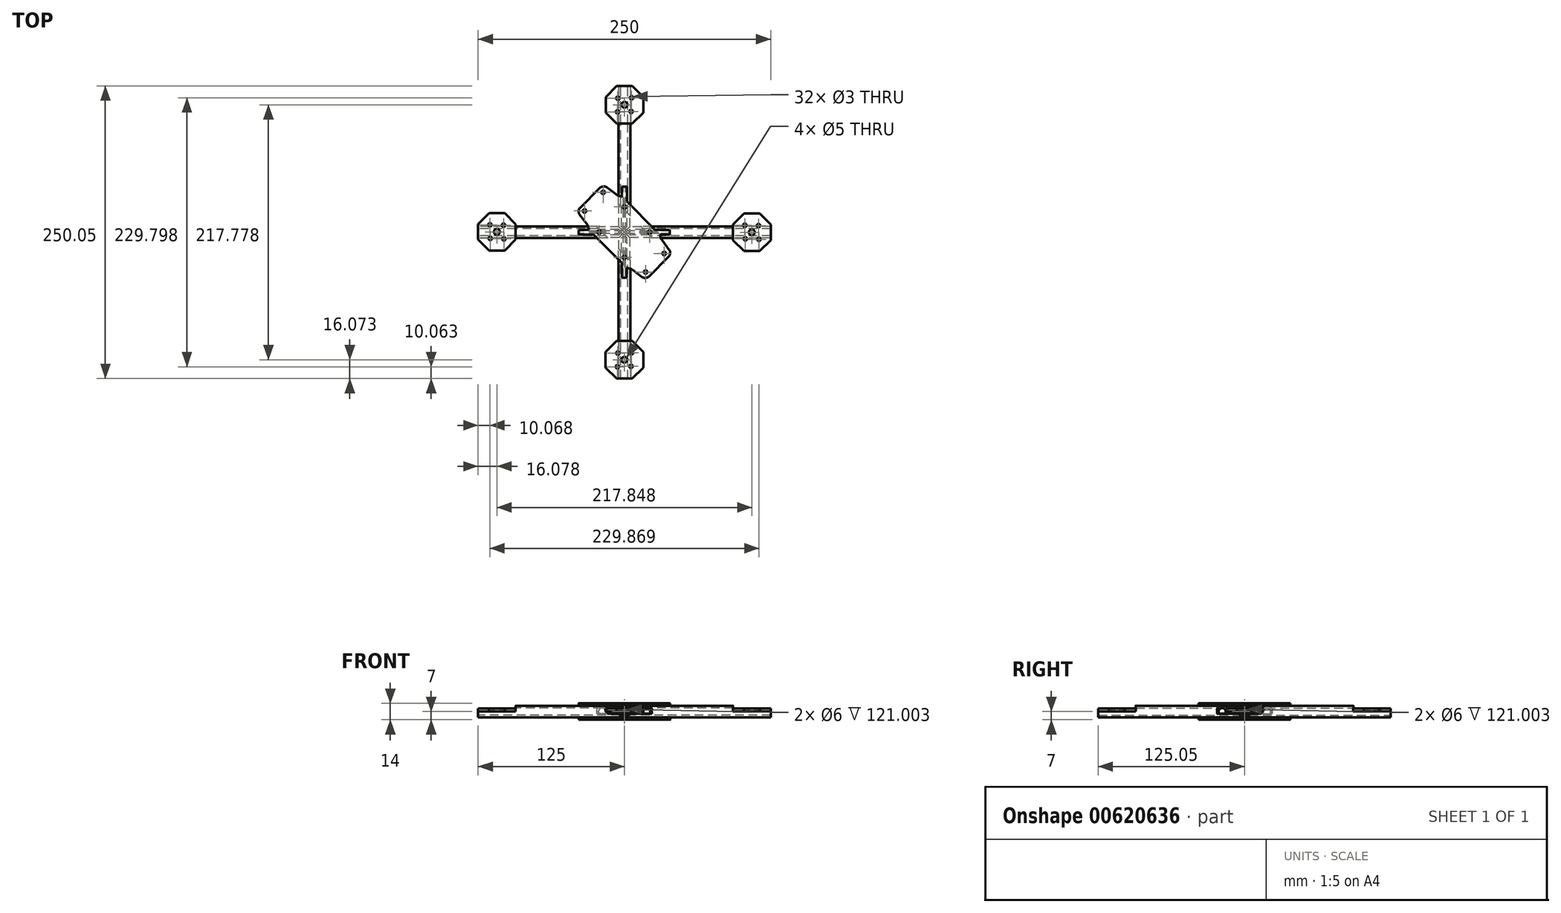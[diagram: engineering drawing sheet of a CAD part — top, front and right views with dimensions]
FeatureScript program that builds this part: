
annotation { "Feature Type Name" : "Feature", "Feature Type Description" : "" }
export const myFeature = defineFeature(function(context is Context, id is Id, definition is map)
    precondition{}
    {
        {
            var Q0;
            Q0=qCreatedBy(makeId("Front.planeOp"),FACE);
            var sketch = newSketch(context, id + "F0", { "sketchPlane" : qUnion([Q0])});
            skCircle(sketch, "E0", {"center": v(0, 0) * mm, "radius": 5 * mm});
            skCircle(sketch, "E1", {"center": v(0, 0) * mm, "radius": 3 * mm});
            skSolve(sketch);
        }
        {
            var Q0;
            Q0 = qSketchRegion(id + "F0", true);
            extrude(context, id + "F1", {"entities" : qUnion([Q0]), "endBound" : BoundingType.SYMMETRIC, "depth" : 250 * mm, "offsetDistance" : 25.4 * mm});
        }
        {
            var Q0;
            Q0=qCreatedBy(makeId("Right.planeOp"),FACE);
            var sketch = newSketch(context, id + "F2", { "sketchPlane" : qUnion([Q0])});
            skCircle(sketch, "E2", {"center": v(0, 0) * mm, "radius": 5 * mm});
            skCircle(sketch, "E3", {"center": v(0, 0) * mm, "radius": 3 * mm});
            skSolve(sketch);
        }
        {
            var Q0;
            Q0 = qSketchRegion(id + "F2", true);
            extrude(context, id + "F3", {"entities" : qUnion([Q0]), "operationType" : NewBodyOperationType.ADD, "endBound" : BoundingType.SYMMETRIC, "depth" : 250 * mm, "offsetDistance" : 25.4 * mm});
        }
        {
            var Q0;
            Q0=qCreatedBy(makeId("Top.planeOp"),FACE);
            var sketch = newSketch(context, id + "F4", { "sketchPlane" : qUnion([Q0])});
            skLineSegment(sketch, "E4.bottom", {"start": v(-92.85, 5) * mm, "end": v(-125.01, 5) * mm});
            skLineSegment(sketch, "E4.top", {"start": v(-92.85, -5) * mm, "end": v(-125.01, -5) * mm});
            skLineSegment(sketch, "E4.left", {"start": v(-92.85, 5) * mm, "end": v(-92.85, -5) * mm});
            skLineSegment(sketch, "E4.right", {"start": v(-125.01, 5) * mm, "end": v(-125.01, -5) * mm});
            skPoint(sketch, "E4.middle", {"position": v(-108.93, 0) * mm});
            skLineSegment(sketch, "E5.bottom", {"start": v(125.05, 5) * mm, "end": v(92.89, 5) * mm});
            skLineSegment(sketch, "E5.top", {"start": v(125.05, -5) * mm, "end": v(92.89, -5) * mm});
            skLineSegment(sketch, "E5.left", {"start": v(125.05, 5) * mm, "end": v(125.05, -5) * mm});
            skLineSegment(sketch, "E5.right", {"start": v(92.89, 5) * mm, "end": v(92.89, -5) * mm});
            skPoint(sketch, "E5.middle", {"position": v(108.97, 0) * mm});
            skLineSegment(sketch, "E6.bottom", {"start": v(-5, -92.95) * mm, "end": v(-5, -125.1) * mm});
            skLineSegment(sketch, "E6.top", {"start": v(5, -92.95) * mm, "end": v(5, -125.1) * mm});
            skLineSegment(sketch, "E6.left", {"start": v(-5, -92.95) * mm, "end": v(5, -92.95) * mm});
            skLineSegment(sketch, "E6.right", {"start": v(-5, -125.1) * mm, "end": v(5, -125.1) * mm});
            skPoint(sketch, "E6.middle", {"position": v(0, -109.03) * mm});
            skLineSegment(sketch, "E7.bottom", {"start": v(-5, 125.15) * mm, "end": v(-5, 93) * mm});
            skLineSegment(sketch, "E7.top", {"start": v(5, 125.15) * mm, "end": v(5, 93) * mm});
            skLineSegment(sketch, "E7.left", {"start": v(-5, 125.15) * mm, "end": v(5, 125.15) * mm});
            skLineSegment(sketch, "E7.right", {"start": v(-5, 93) * mm, "end": v(5, 93) * mm});
            skPoint(sketch, "E7.middle", {"position": v(0, 109.07) * mm});
            skSolve(sketch);
        }
        {
            var Q0;
            Q0 = qSketchRegion(id + "F4", true);
            extrude(context, id + "F5", {"entities" : qUnion([Q0]), "operationType" : NewBodyOperationType.REMOVE, "depth" : 5 * mm, "offsetDistance" : 25.4 * mm});
        }
        {
            var Q0;
            Q0=qCreatedBy(makeId("Top.planeOp"),FACE);
            var sketch = newSketch(context, id + "F6", { "sketchPlane" : qUnion([Q0])});
            skCircle(sketch, "E8", {"center": v(-108.92, 0.28) * mm, "radius": 14 * mm, "construction": true});
            skLineSegment(sketch, "E9", {"start": v(-118.82, 10.18) * mm, "end": v(-108.92, 0.28) * mm, "construction": true});
            skLineSegment(sketch, "E10", {"start": v(-108.92, 0.28) * mm, "end": v(-118.82, -9.62) * mm, "construction": true});
            skCircle(sketch, "E11", {"center": v(-103.26, 5.94) * mm, "radius": 1.5 * mm});
            skCircle(sketch, "E12", {"center": v(-114.58, -5.37) * mm, "radius": 1.5 * mm});
            skLineSegment(sketch, "E13", {"start": v(-108.92, 0.28) * mm, "end": v(-99.02, -9.62) * mm, "construction": true});
            skLineSegment(sketch, "E14", {"start": v(-108.92, 0.28) * mm, "end": v(-99.02, 10.18) * mm, "construction": true});
            skCircle(sketch, "E15", {"center": v(-114.93, 6.3) * mm, "radius": 1.5 * mm});
            skCircle(sketch, "E16", {"center": v(-102.91, -5.73) * mm, "radius": 1.5 * mm});
            skCircle(sketch, "E17", {"center": v(-108.92, 0.28) * mm, "radius": 2.5 * mm});
            skCircle(sketch, "E18.cCircle", {"center": v(-108.92, 0.28) * mm, "radius": 16.07 * mm, "construction": true});
            skLineSegment(sketch, "E18.0", {"start": v(-125, -6.38) * mm, "end": v(-125, 6.94) * mm});
            skLineSegment(sketch, "E18.1", {"start": v(-125, 6.94) * mm, "end": v(-115.58, 16.35) * mm});
            skLineSegment(sketch, "E18.2", {"start": v(-115.58, 16.35) * mm, "end": v(-102.26, 16.35) * mm});
            skLineSegment(sketch, "E18.3", {"start": v(-102.26, 16.35) * mm, "end": v(-92.85, 6.94) * mm});
            skLineSegment(sketch, "E18.4", {"start": v(-92.85, 6.94) * mm, "end": v(-92.85, -6.38) * mm});
            skLineSegment(sketch, "E18.5", {"start": v(-92.85, -6.38) * mm, "end": v(-102.26, -15.8) * mm});
            skLineSegment(sketch, "E18.6", {"start": v(-102.26, -15.8) * mm, "end": v(-115.58, -15.8) * mm});
            skLineSegment(sketch, "E18.7", {"start": v(-115.58, -15.8) * mm, "end": v(-125, -6.38) * mm});
            skPoint(sketch, "E18.0.midPoint", {"position": v(-125, 0.28) * mm});
            skCircle(sketch, "E19", {"center": v(0.1, 108.8) * mm, "radius": 14 * mm, "construction": true});
            skLineSegment(sketch, "E20", {"start": v(10, 118.7) * mm, "end": v(0.1, 108.8) * mm, "construction": true});
            skLineSegment(sketch, "E21", {"start": v(0.1, 108.8) * mm, "end": v(-9.8, 118.7) * mm, "construction": true});
            skCircle(sketch, "E22", {"center": v(5.76, 103.14) * mm, "radius": 1.5 * mm});
            skCircle(sketch, "E23", {"center": v(-5.55, 114.46) * mm, "radius": 1.5 * mm});
            skLineSegment(sketch, "E24", {"start": v(0.1, 108.8) * mm, "end": v(-9.8, 98.9) * mm, "construction": true});
            skLineSegment(sketch, "E25", {"start": v(0.1, 108.8) * mm, "end": v(10, 98.9) * mm, "construction": true});
            skCircle(sketch, "E26", {"center": v(6.12, 114.81) * mm, "radius": 1.5 * mm});
            skCircle(sketch, "E27", {"center": v(-5.9, 102.8) * mm, "radius": 1.5 * mm});
            skCircle(sketch, "E28", {"center": v(0.1, 108.8) * mm, "radius": 2.5 * mm});
            skCircle(sketch, "E29.cCircle", {"center": v(0.1, 108.8) * mm, "radius": 16.07 * mm, "construction": true});
            skLineSegment(sketch, "E29.0", {"start": v(-6.55, 124.87) * mm, "end": v(6.76, 124.87) * mm});
            skLineSegment(sketch, "E29.1", {"start": v(6.76, 124.87) * mm, "end": v(16.18, 115.46) * mm});
            skLineSegment(sketch, "E29.2", {"start": v(16.18, 115.46) * mm, "end": v(16.18, 102.14) * mm});
            skLineSegment(sketch, "E29.3", {"start": v(16.18, 102.14) * mm, "end": v(6.76, 92.73) * mm});
            skLineSegment(sketch, "E29.4", {"start": v(6.76, 92.73) * mm, "end": v(-6.55, 92.73) * mm});
            skLineSegment(sketch, "E29.5", {"start": v(-6.55, 92.73) * mm, "end": v(-15.97, 102.14) * mm});
            skLineSegment(sketch, "E29.6", {"start": v(-15.97, 102.14) * mm, "end": v(-15.97, 115.46) * mm});
            skLineSegment(sketch, "E29.7", {"start": v(-15.97, 115.46) * mm, "end": v(-6.55, 124.87) * mm});
            skPoint(sketch, "E29.0.midPoint", {"position": v(0.1, 124.87) * mm});
            skCircle(sketch, "E30", {"center": v(0.03, -108.98) * mm, "radius": 14 * mm, "construction": true});
            skLineSegment(sketch, "E31", {"start": v(-9.87, -118.88) * mm, "end": v(0.03, -108.98) * mm, "construction": true});
            skLineSegment(sketch, "E32", {"start": v(0.03, -108.98) * mm, "end": v(9.93, -118.88) * mm, "construction": true});
            skCircle(sketch, "E33", {"center": v(-5.63, -103.32) * mm, "radius": 1.5 * mm});
            skCircle(sketch, "E34", {"center": v(5.68, -114.63) * mm, "radius": 1.5 * mm});
            skLineSegment(sketch, "E35", {"start": v(0.03, -108.98) * mm, "end": v(9.93, -99.08) * mm, "construction": true});
            skLineSegment(sketch, "E36", {"start": v(0.03, -108.98) * mm, "end": v(-9.87, -99.08) * mm, "construction": true});
            skCircle(sketch, "E37", {"center": v(-5.98, -114.99) * mm, "radius": 1.5 * mm});
            skCircle(sketch, "E38", {"center": v(6.04, -102.97) * mm, "radius": 1.5 * mm});
            skCircle(sketch, "E39", {"center": v(0.03, -108.98) * mm, "radius": 2.5 * mm});
            skCircle(sketch, "E40.cCircle", {"center": v(0.03, -108.98) * mm, "radius": 16.07 * mm, "construction": true});
            skLineSegment(sketch, "E40.0", {"start": v(6.69, -125.05) * mm, "end": v(-6.63, -125.05) * mm});
            skLineSegment(sketch, "E40.1", {"start": v(-6.63, -125.05) * mm, "end": v(-16.05, -115.63) * mm});
            skLineSegment(sketch, "E40.2", {"start": v(-16.05, -115.63) * mm, "end": v(-16.05, -102.32) * mm});
            skLineSegment(sketch, "E40.3", {"start": v(-16.05, -102.32) * mm, "end": v(-6.63, -92.9) * mm});
            skLineSegment(sketch, "E40.4", {"start": v(-6.63, -92.9) * mm, "end": v(6.69, -92.9) * mm});
            skLineSegment(sketch, "E40.5", {"start": v(6.69, -92.9) * mm, "end": v(16.1, -102.32) * mm});
            skLineSegment(sketch, "E40.6", {"start": v(16.1, -102.32) * mm, "end": v(16.1, -115.63) * mm});
            skLineSegment(sketch, "E40.7", {"start": v(16.1, -115.63) * mm, "end": v(6.69, -125.05) * mm});
            skPoint(sketch, "E40.0.midPoint", {"position": v(0.03, -125.05) * mm});
            skCircle(sketch, "E41", {"center": v(108.93, -0.08) * mm, "radius": 14 * mm, "construction": true});
            skLineSegment(sketch, "E42", {"start": v(118.83, -9.97) * mm, "end": v(108.93, -0.08) * mm, "construction": true});
            skLineSegment(sketch, "E43", {"start": v(108.93, -0.08) * mm, "end": v(118.83, 9.82) * mm, "construction": true});
            skCircle(sketch, "E44", {"center": v(103.27, -5.73) * mm, "radius": 1.5 * mm});
            skCircle(sketch, "E45", {"center": v(114.58, 5.58) * mm, "radius": 1.5 * mm});
            skLineSegment(sketch, "E46", {"start": v(108.93, -0.08) * mm, "end": v(99.03, 9.82) * mm, "construction": true});
            skLineSegment(sketch, "E47", {"start": v(108.93, -0.08) * mm, "end": v(99.03, -9.97) * mm, "construction": true});
            skCircle(sketch, "E48", {"center": v(114.94, -6.09) * mm, "radius": 1.5 * mm});
            skCircle(sketch, "E49", {"center": v(102.92, 5.93) * mm, "radius": 1.5 * mm});
            skCircle(sketch, "E50", {"center": v(108.93, -0.08) * mm, "radius": 2.5 * mm});
            skCircle(sketch, "E51.cCircle", {"center": v(108.93, -0.08) * mm, "radius": 16.07 * mm, "construction": true});
            skLineSegment(sketch, "E51.0", {"start": v(125, 6.58) * mm, "end": v(125, -6.73) * mm});
            skLineSegment(sketch, "E51.1", {"start": v(125, -6.73) * mm, "end": v(115.58, -16.15) * mm});
            skLineSegment(sketch, "E51.2", {"start": v(115.58, -16.15) * mm, "end": v(102.27, -16.15) * mm});
            skLineSegment(sketch, "E51.3", {"start": v(102.27, -16.15) * mm, "end": v(92.85, -6.73) * mm});
            skLineSegment(sketch, "E51.4", {"start": v(92.85, -6.73) * mm, "end": v(92.85, 6.58) * mm});
            skLineSegment(sketch, "E51.5", {"start": v(92.85, 6.58) * mm, "end": v(102.27, 16) * mm});
            skLineSegment(sketch, "E51.6", {"start": v(102.27, 16) * mm, "end": v(115.58, 16) * mm});
            skLineSegment(sketch, "E51.7", {"start": v(115.58, 16) * mm, "end": v(125, 6.58) * mm});
            skPoint(sketch, "E51.0.midPoint", {"position": v(125, -0.08) * mm});
            skSolve(sketch);
        }
        {
            var Q0;
            Q0 = qSketchRegion(id + "F6", true);
            var Q1;
            Q1 = qConstructionFilter(qBodyType(qCreatedBy(id + "F6" ,EDGE), BodyType.WIRE), ConstructionObject.NO);
            extrude(context, id + "F7", {"entities" : qUnion([Q0]), "surfaceEntities" : qUnion([Q1]), "depth" : 2.5 * mm, "offsetDistance" : 25.4 * mm});
        }
        {
            var Q0;
            Q0=qCreatedBy(makeId("Top.planeOp"),FACE);
            var sketch = newSketch(context, id + "F8", { "sketchPlane" : qUnion([Q0])});
            skPoint(sketch, "E52.middle", {"position": v(0.02, 0) * mm});
            skLineSegment(sketch, "E53", {"start": v(2.11, -30.38) * mm, "end": v(6.01, -31.5) * mm});
            skLineSegment(sketch, "E54", {"start": v(6.01, -31.5) * mm, "end": v(18.15, -40.58) * mm});
            skPoint(sketch, "E55.endSnap0", {"position": v(29.37, -29.38) * mm});
            skLineSegment(sketch, "E56", {"start": v(29.37, -29.38) * mm, "end": v(0.02, 0) * mm, "construction": true});
            skLineSegment(sketch, "E57", {"start": v(18.15, -40.58) * mm, "end": v(29.37, -29.38) * mm});
            skLineSegment(sketch, "E58", {"start": v(0.02, 0) * mm, "end": v(-14.13, -14.13) * mm, "construction": true});
            skLineSegment(sketch, "E59.MirrorCS", {"start": v(30.4, -2.12) * mm, "end": v(31.5, -6.02) * mm});
            skLineSegment(sketch, "E60.MirrorCS", {"start": v(31.5, -6.02) * mm, "end": v(40.59, -18.17) * mm});
            skLineSegment(sketch, "E61.MirrorCS", {"start": v(40.59, -18.17) * mm, "end": v(29.37, -29.38) * mm});
            skCircle(sketch, "E62", {"center": v(0.01, -21.57) * mm, "radius": 1.5 * mm});
            skCircle(sketch, "E63.MirrorC", {"center": v(21.6, -0.01) * mm, "radius": 1.5 * mm});
            skCircle(sketch, "E64", {"center": v(18.15, -34.02) * mm, "radius": 1.5 * mm});
            skCircle(sketch, "E65.MirrorC", {"center": v(34.02, -18.16) * mm, "radius": 1.5 * mm});
            skLineSegment(sketch, "E66.MirrorCS", {"start": v(0.02, 0) * mm, "end": v(14.17, 14.13) * mm, "construction": true});
            skLineSegment(sketch, "E67", {"start": v(-14.13, -14.13) * mm, "end": v(-2.09, -26.19) * mm});
            skLineSegment(sketch, "E68.MirrorCS", {"start": v(14.17, 14.13) * mm, "end": v(26.21, 2.08) * mm});
            skLineSegment(sketch, "E69.MirrorCS", {"start": v(-5.96, 31.5) * mm, "end": v(-18.1, 40.58) * mm});
            skLineSegment(sketch, "E70.MirrorCS", {"start": v(-29.32, 29.38) * mm, "end": v(0.02, 0) * mm, "construction": true});
            skLineSegment(sketch, "E71.MirrorCS", {"start": v(-30.35, 2.12) * mm, "end": v(-31.46, 6.02) * mm});
            skLineSegment(sketch, "E72.MirrorCS", {"start": v(14.17, 14.13) * mm, "end": v(2.13, 26.19) * mm});
            skCircle(sketch, "E73.MirrorC", {"center": v(0.04, 21.57) * mm, "radius": 1.5 * mm});
            skCircle(sketch, "E74.MirrorC", {"center": v(-21.54, 0.01) * mm, "radius": 1.5 * mm});
            skPoint(sketch, "E75.MirrorP", {"position": v(-29.32, 29.38) * mm});
            skCircle(sketch, "E76.MirrorC", {"center": v(-33.97, 18.16) * mm, "radius": 1.5 * mm});
            skLineSegment(sketch, "E77.MirrorCS", {"start": v(-40.54, 18.17) * mm, "end": v(-29.32, 29.38) * mm});
            skCircle(sketch, "E78.MirrorC", {"center": v(-18.1, 34.02) * mm, "radius": 1.5 * mm});
            skLineSegment(sketch, "E79.MirrorCS", {"start": v(-31.46, 6.02) * mm, "end": v(-40.54, 18.17) * mm});
            skLineSegment(sketch, "E80.MirrorCS", {"start": v(-14.13, -14.13) * mm, "end": v(-26.17, -2.08) * mm});
            skLineSegment(sketch, "E81.MirrorCS", {"start": v(-2.06, 30.38) * mm, "end": v(-5.96, 31.5) * mm});
            skLineSegment(sketch, "E82.MirrorCS", {"start": v(-18.1, 40.58) * mm, "end": v(-29.32, 29.38) * mm});
            skLineSegment(sketch, "E83", {"start": v(-30.35, 2.12) * mm, "end": v(2.11, -30.38) * mm});
            skLineSegment(sketch, "E84", {"start": v(-2.06, 30.38) * mm, "end": v(30.4, -2.12) * mm});
            skSolve(sketch);
        }
        {
            var Q0;
            Q0=qCreatedBy(makeId("Top.planeOp"),FACE);
            var sketch = newSketch(context, id + "F9", { "sketchPlane" : qUnion([Q0])});
            skPoint(sketch, "E85.middle", {"position": v(0, 0) * mm});
            skLineSegment(sketch, "E86.top", {"start": v(-2.12, -38.87) * mm, "end": v(2.08, -38.87) * mm});
            skLineSegment(sketch, "E87", {"start": v(-2.12, -38.87) * mm, "end": v(-2.11, -26.19) * mm});
            skLineSegment(sketch, "E88", {"start": v(2.08, -38.87) * mm, "end": v(2.09, -30.38) * mm});
            skLineSegment(sketch, "E89", {"start": v(2.09, -30.38) * mm, "end": v(5.99, -31.5) * mm});
            skLineSegment(sketch, "E90", {"start": v(5.99, -31.5) * mm, "end": v(18.12, -40.58) * mm});
            skPoint(sketch, "E91.endSnap0", {"position": v(29.34, -29.38) * mm});
            skLineSegment(sketch, "E92", {"start": v(29.34, -29.38) * mm, "end": v(0, 0) * mm, "construction": true});
            skLineSegment(sketch, "E93", {"start": v(18.12, -40.58) * mm, "end": v(29.34, -29.38) * mm});
            skLineSegment(sketch, "E94", {"start": v(0, 0) * mm, "end": v(-14.15, -14.13) * mm, "construction": true});
            skLineSegment(sketch, "E95", {"start": v(0, 0) * mm, "end": v(-0.02, -38.87) * mm, "construction": true});
            skLineSegment(sketch, "E96.MirrorCS", {"start": v(38.87, 2.08) * mm, "end": v(26.2, 2.08) * mm});
            skLineSegment(sketch, "E97.MirrorCS", {"start": v(0, 0) * mm, "end": v(38.87, -0.02) * mm, "construction": true});
            skLineSegment(sketch, "E98.MirrorCS", {"start": v(38.87, 2.08) * mm, "end": v(38.87, -2.12) * mm});
            skLineSegment(sketch, "E99.MirrorCS", {"start": v(38.87, -2.12) * mm, "end": v(30.37, -2.12) * mm});
            skLineSegment(sketch, "E100.MirrorCS", {"start": v(30.37, -2.12) * mm, "end": v(31.48, -6.02) * mm});
            skLineSegment(sketch, "E101.MirrorCS", {"start": v(31.48, -6.02) * mm, "end": v(40.56, -18.17) * mm});
            skLineSegment(sketch, "E102.MirrorCS", {"start": v(40.56, -18.17) * mm, "end": v(29.34, -29.38) * mm});
            skCircle(sketch, "E103", {"center": v(-0.01, -21.57) * mm, "radius": 1.5 * mm});
            skCircle(sketch, "E104.MirrorC", {"center": v(21.57, -0.01) * mm, "radius": 1.5 * mm});
            skCircle(sketch, "E105", {"center": v(18.12, -34.02) * mm, "radius": 1.5 * mm});
            skCircle(sketch, "E106.MirrorC", {"center": v(34, -18.16) * mm, "radius": 1.5 * mm});
            skLineSegment(sketch, "E107.MirrorCS", {"start": v(0, 0) * mm, "end": v(14.15, 14.13) * mm, "construction": true});
            skLineSegment(sketch, "E108", {"start": v(-14.15, -14.13) * mm, "end": v(-2.11, -26.19) * mm});
            skLineSegment(sketch, "E109.MirrorCS", {"start": v(14.15, 14.13) * mm, "end": v(26.2, 2.08) * mm});
            skLineSegment(sketch, "E110.MirrorCS", {"start": v(2.12, 38.87) * mm, "end": v(-2.08, 38.87) * mm});
            skLineSegment(sketch, "E111.MirrorCS", {"start": v(-38.87, -2.08) * mm, "end": v(-38.87, 2.12) * mm});
            skLineSegment(sketch, "E112.MirrorCS", {"start": v(2.12, 38.87) * mm, "end": v(2.11, 26.19) * mm});
            skLineSegment(sketch, "E113.MirrorCS", {"start": v(-5.99, 31.5) * mm, "end": v(-18.12, 40.58) * mm});
            skLineSegment(sketch, "E114.MirrorCS", {"start": v(-29.34, 29.38) * mm, "end": v(0, 0) * mm, "construction": true});
            skLineSegment(sketch, "E115.MirrorCS", {"start": v(-30.37, 2.12) * mm, "end": v(-31.48, 6.02) * mm});
            skLineSegment(sketch, "E116.MirrorCS", {"start": v(14.15, 14.13) * mm, "end": v(2.11, 26.19) * mm});
            skLineSegment(sketch, "E117.MirrorCS", {"start": v(-2.08, 38.87) * mm, "end": v(-2.09, 30.38) * mm});
            skCircle(sketch, "E118.MirrorC", {"center": v(0.01, 21.57) * mm, "radius": 1.5 * mm});
            skCircle(sketch, "E119.MirrorC", {"center": v(-21.57, 0.01) * mm, "radius": 1.5 * mm});
            skPoint(sketch, "E120.MirrorP", {"position": v(-29.34, 29.38) * mm});
            skLineSegment(sketch, "E121.MirrorCS", {"start": v(0, 0) * mm, "end": v(0.02, 38.87) * mm, "construction": true});
            skCircle(sketch, "E122.MirrorC", {"center": v(-34, 18.16) * mm, "radius": 1.5 * mm});
            skLineSegment(sketch, "E123.MirrorCS", {"start": v(-40.56, 18.17) * mm, "end": v(-29.34, 29.38) * mm});
            skCircle(sketch, "E124.MirrorC", {"center": v(-18.12, 34.02) * mm, "radius": 1.5 * mm});
            skLineSegment(sketch, "E125.MirrorCS", {"start": v(-31.48, 6.02) * mm, "end": v(-40.56, 18.17) * mm});
            skLineSegment(sketch, "E126.MirrorCS", {"start": v(-14.15, -14.13) * mm, "end": v(-26.2, -2.08) * mm});
            skLineSegment(sketch, "E127.MirrorCS", {"start": v(-2.09, 30.38) * mm, "end": v(-5.99, 31.5) * mm});
            skLineSegment(sketch, "E128.MirrorCS", {"start": v(-18.12, 40.58) * mm, "end": v(-29.34, 29.38) * mm});
            skLineSegment(sketch, "E129.MirrorCS", {"start": v(-38.87, -2.08) * mm, "end": v(-26.2, -2.08) * mm});
            skLineSegment(sketch, "E130.MirrorCS", {"start": v(-38.87, 2.12) * mm, "end": v(-30.37, 2.12) * mm});
            skLineSegment(sketch, "E131.MirrorCS", {"start": v(0, 0) * mm, "end": v(-38.87, 0.02) * mm, "construction": true});
            skSolve(sketch);
        }
        {
            var Q0;
            Q0 = qSketchRegion(id + "F9", true);
            extrude(context, id + "F10", {"entities" : qUnion([Q0]), "operationType" : NewBodyOperationType.ADD, "depth" : 7 * mm, "offsetDistance" : 25 * mm, "hasSecondDirection" : true, "secondDirectionOppositeDirection" : false, "secondDirectionDepth" : 4.9 * mm});
        }
        {
            var Q0;
            Q0 = qSketchRegion(id + "F8", true);
            extrude(context, id + "F11", {"entities" : qUnion([Q0]), "operationType" : NewBodyOperationType.ADD, "oppositeDirection" : true, "depth" : 7 * mm, "offsetDistance" : 25 * mm, "hasSecondDirection" : true, "secondDirectionOppositeDirection" : true, "secondDirectionDepth" : 4.9 * mm});
        }
        {
            var Q0;
            Q0=qCreatedBy(makeId("Top.planeOp"),FACE);
            var sketch = newSketch(context, id + "F12", { "sketchPlane" : qUnion([Q0])});
            skPoint(sketch, "E132.middle", {"position": v(0, 0) * mm});
            skLineSegment(sketch, "E133.bottom", {"start": v(23.69, -4.6) * mm, "end": v(-4.6, 23.69) * mm});
            skLineSegment(sketch, "E133.top", {"start": v(4.6, -23.69) * mm, "end": v(-23.69, 4.6) * mm});
            skLineSegment(sketch, "E133.left", {"start": v(23.69, -4.6) * mm, "end": v(4.6, -23.69) * mm});
            skLineSegment(sketch, "E133.right", {"start": v(-4.6, 23.69) * mm, "end": v(-23.69, 4.6) * mm});
            skSolve(sketch);
        }
        {
            var Q0;
            Q0=makeQuery(id+"F11.opExtrude","SWEPT_EDGE",EDGE,{"disambiguationData":[OSD([sQuery(id+"F8.wireOp",EDGE,"E77.MirrorCS"),sQuery(id+"F8.wireOp",EDGE,"E79.MirrorCS")])]});
            var Q1;
            Q1=makeQuery(id+"F11.opExtrude","SWEPT_EDGE",EDGE,{"disambiguationData":[OSD([sQuery(id+"F8.wireOp",EDGE,"E71.MirrorCS"),sQuery(id+"F8.wireOp",EDGE,"E83")])]});
            var Q2;
            Q2=makeQuery(id+"F11.opExtrude","SWEPT_EDGE",EDGE,{"disambiguationData":[OSD([sQuery(id+"F8.wireOp",EDGE,"E53"),sQuery(id+"F8.wireOp",EDGE,"E83")])]});
            var Q3;
            Q3=makeQuery(id+"F11.opExtrude","SWEPT_EDGE",EDGE,{"disambiguationData":[OSD([sQuery(id+"F8.wireOp",EDGE,"E54"),sQuery(id+"F8.wireOp",EDGE,"E57")])]});
            var Q4;
            Q4=makeQuery(id+"F10.opExtrude","SWEPT_EDGE",EDGE,{"disambiguationData":[OSD([sQuery(id+"F9.wireOp",EDGE,"E90"),sQuery(id+"F9.wireOp",EDGE,"E93")])]});
            var Q5;
            Q5=makeQuery(id+"F10.opExtrude","SWEPT_EDGE",EDGE,{"disambiguationData":[OSD([sQuery(id+"F9.wireOp",EDGE,"E89"),sQuery(id+"F9.wireOp",EDGE,"E90")])]});
            var Q6;
            Q6=makeQuery(id+"F10.opExtrude","SWEPT_EDGE",EDGE,{"disambiguationData":[OSD([sQuery(id+"F9.wireOp",EDGE,"E101.MirrorCS"),sQuery(id+"F9.wireOp",EDGE,"E102.MirrorCS")])]});
            var Q7;
            Q7=makeQuery(id+"F10.opExtrude","SWEPT_EDGE",EDGE,{"disambiguationData":[OSD([sQuery(id+"F9.wireOp",EDGE,"E100.MirrorCS"),sQuery(id+"F9.wireOp",EDGE,"E101.MirrorCS")])]});
            var Q8;
            Q8=makeQuery(id+"F11.opExtrude","SWEPT_EDGE",EDGE,{"disambiguationData":[OSD([sQuery(id+"F8.wireOp",EDGE,"E60.MirrorCS"),sQuery(id+"F8.wireOp",EDGE,"E61.MirrorCS")])]});
            var Q9;
            Q9=makeQuery(id+"F11.opExtrude","SWEPT_EDGE",EDGE,{"disambiguationData":[OSD([sQuery(id+"F8.wireOp",EDGE,"E59.MirrorCS"),sQuery(id+"F8.wireOp",EDGE,"E60.MirrorCS")])]});
            var Q10;
            Q10=makeQuery(id+"F11.opExtrude","SWEPT_EDGE",EDGE,{"disambiguationData":[OSD([sQuery(id+"F8.wireOp",EDGE,"E59.MirrorCS"),sQuery(id+"F8.wireOp",EDGE,"E84")])]});
            var Q11;
            Q11=makeQuery(id+"F10.opExtrude","SWEPT_EDGE",EDGE,{"disambiguationData":[OSD([sQuery(id+"F9.wireOp",EDGE,"E123.MirrorCS"),sQuery(id+"F9.wireOp",EDGE,"E125.MirrorCS")])]});
            var Q12;
            Q12=makeQuery(id+"F11.opExtrude","SWEPT_EDGE",EDGE,{"disambiguationData":[OSD([sQuery(id+"F8.wireOp",EDGE,"E69.MirrorCS"),sQuery(id+"F8.wireOp",EDGE,"E82.MirrorCS")])]});
            var Q13;
            Q13=makeQuery(id+"F10.opExtrude","SWEPT_EDGE",EDGE,{"disambiguationData":[OSD([sQuery(id+"F9.wireOp",EDGE,"E113.MirrorCS"),sQuery(id+"F9.wireOp",EDGE,"E128.MirrorCS")])]});
            fillet(context, id + "F13", {"entities" : qUnion([Q0, Q1, Q2, Q3, Q4, Q5, Q6, Q7, Q8, Q9, Q10, Q11, Q12, Q13]), "radius" : 4.5 * mm, "tangentPropagation" : true, "allowEdgeOverflow" : false});
        }
        {
            var Q0;
            Q0 = qSketchRegion(id + "F12", true);
            extrude(context, id + "F14", {"entities" : qUnion([Q0]), "operationType" : NewBodyOperationType.REMOVE, "oppositeDirection" : true, "depth" : -4.9 * mm, "offsetDistance" : 25 * mm});
        }
        {
            var Q0;
            Q0 = qSketchRegion(id + "F12", true);
            extrude(context, id + "F15", {"entities" : qUnion([Q0]), "operationType" : NewBodyOperationType.REMOVE, "oppositeDirection" : true, "depth" : 1.8 * mm, "offsetDistance" : 25 * mm});
        }
    });
